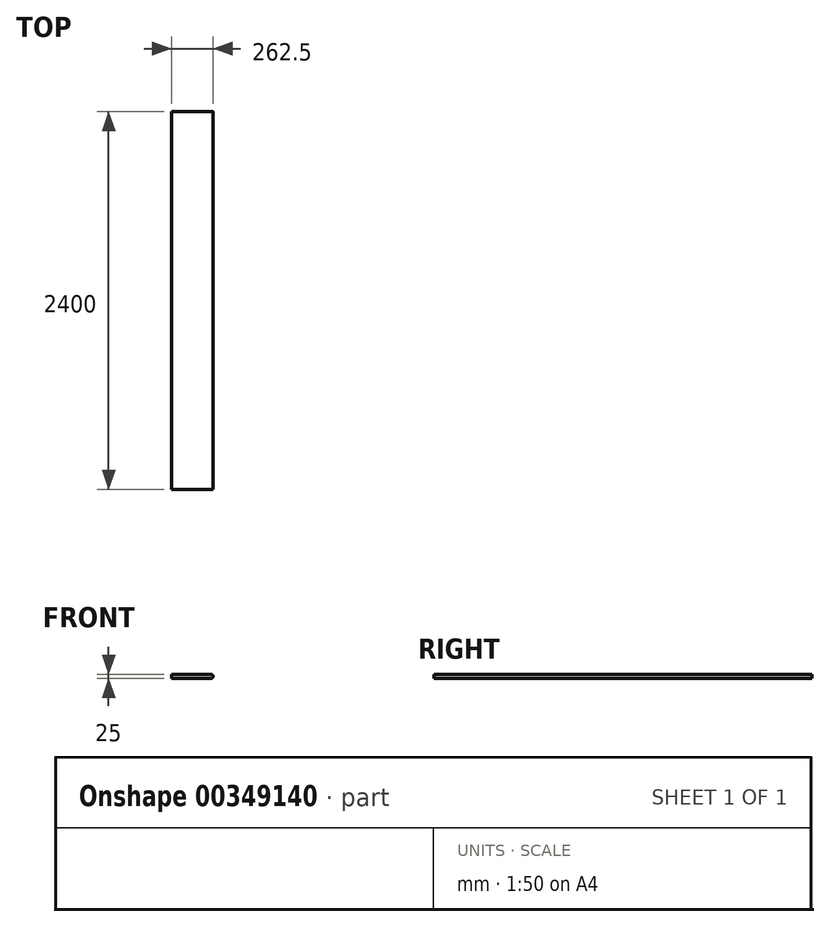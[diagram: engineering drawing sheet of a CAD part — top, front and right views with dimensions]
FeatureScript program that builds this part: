
annotation { "Feature Type Name" : "Feature", "Feature Type Description" : "" }
export const myFeature = defineFeature(function(context is Context, id is Id, definition is map)
    precondition{}
    {
        {
            var Q0;
            Q0=qCreatedBy(makeId("Front.planeOp"),FACE);
            var sketch = newSketch(context, id + "F0", { "sketchPlane" : qUnion([Q0])});
            skLineSegment(sketch, "E0.bottom", {"start": v(0, 0) * mm, "end": v(250, 0) * mm});
            skLineSegment(sketch, "E0.top", {"start": v(0, 25) * mm, "end": v(250, 25) * mm});
            skLineSegment(sketch, "E0.left", {"start": v(0, 0) * mm, "end": v(0, 25) * mm});
            skArc(sketch, "E1", {"start": v(250, 0) * mm, "mid": v(262.5, 12.5) * mm, "end": v(250, 25) * mm});
            skSolve(sketch);
        }
        {
            var Q0;
            Q0=makeQuery(id+"F0.imprint","IMPRINT",FACE,{"disambiguationData":[TD([[makeQuery(id+"F0.imprint","IMPRINT",EDGE,{"derivedFrom":sQuery(id+"F0.wireOp",EDGE,"E0.bottom")}),1.0]])]});
            extrude(context, id + "F1", {"entities" : qUnion([Q0]), "depth" : 2400 * mm});
        }
    });
